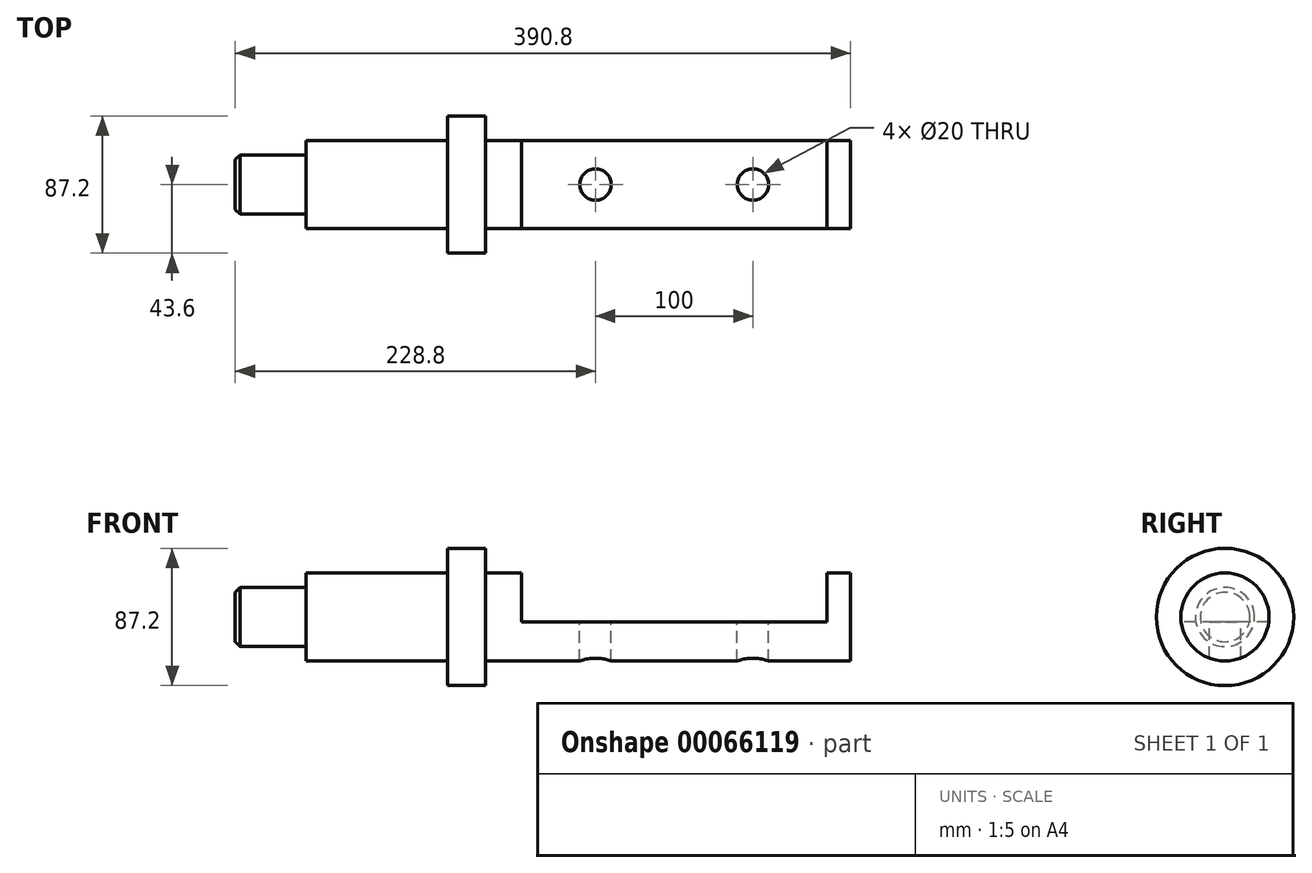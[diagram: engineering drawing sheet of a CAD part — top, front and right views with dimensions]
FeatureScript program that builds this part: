
annotation { "Feature Type Name" : "Feature", "Feature Type Description" : "" }
export const myFeature = defineFeature(function(context is Context, id is Id, definition is map)
    precondition{}
    {
        {
            var Q0;
            Q0=qCreatedBy(makeId("Front.planeOp"),FACE);
            var sketch = newSketch(context, id + "F0", { "sketchPlane" : qUnion([Q0])});
            skLineSegment(sketch, "E0", {"start": v(-158.8, 0) * mm, "end": v(-158.8, 18.75) * mm});
            skLineSegment(sketch, "E1", {"start": v(-158.8, 18.75) * mm, "end": v(-113.8, 18.75) * mm});
            skLineSegment(sketch, "E2", {"start": v(-113.8, 18.75) * mm, "end": v(-113.8, 28) * mm});
            skLineSegment(sketch, "E3", {"start": v(-113.8, 28) * mm, "end": v(-24, 28) * mm});
            skLineSegment(sketch, "E4", {"start": v(-24, 28) * mm, "end": v(-24, 43.6) * mm});
            skLineSegment(sketch, "E5", {"start": v(-24, 43.6) * mm, "end": v(0, 43.6) * mm});
            skLineSegment(sketch, "E6", {"start": v(0, 43.6) * mm, "end": v(0, 28) * mm});
            skLineSegment(sketch, "E7", {"start": v(0, 28) * mm, "end": v(232, 28) * mm});
            skLineSegment(sketch, "E8", {"start": v(232, 28) * mm, "end": v(232, 0) * mm});
            skLineSegment(sketch, "E9", {"start": v(232, 0) * mm, "end": v(-158.8, 0) * mm});
            skSolve(sketch);
        }
        {
            var Q0;
            Q0=makeQuery(id+"F0.imprint","IMPRINT",FACE,{"disambiguationData":[TD([[makeQuery(id+"F0.imprint","IMPRINT",EDGE,{"derivedFrom":sQuery(id+"F0.wireOp",EDGE,"E0")}),-1.0]])]});
            var Q1;
            Q1=sQuery(id+"F0.wireOp",EDGE,"E9");
            revolve(context, id + "F1", {"entities" : qUnion([Q0]), "axis" : qUnion([Q1]), "revolveType" : RevolveType.FULL});
        }
        {
            var Q0;
            Q0=qCreatedBy(makeId("Front.planeOp"),FACE);
            var sketch = newSketch(context, id + "F2", { "sketchPlane" : qUnion([Q0])});
            skLineSegment(sketch, "E10.bottom", {"start": v(23.1, 41.08) * mm, "end": v(216.9, 41.08) * mm});
            skLineSegment(sketch, "E10.top", {"start": v(23.1, -3.1) * mm, "end": v(216.9, -3.1) * mm});
            skLineSegment(sketch, "E10.left", {"start": v(23.1, 41.08) * mm, "end": v(23.1, -3.1) * mm});
            skLineSegment(sketch, "E10.right", {"start": v(216.9, 41.08) * mm, "end": v(216.9, -3.1) * mm});
            skLineSegment(sketch, "E11.0", {"start": v(232, 28) * mm, "end": v(232, -28) * mm, "construction": true});
            skSolve(sketch);
        }
        {
            var Q0;
            Q0=makeQuery(id+"F2.imprint","IMPRINT",FACE,{"disambiguationData":[TD([[makeQuery(id+"F2.imprint","IMPRINT",EDGE,{"derivedFrom":sQuery(id+"F2.wireOp",EDGE,"E10.bottom")}),-1.0]])]});
            extrude(context, id + "F3", {"entities" : qUnion([Q0]), "operationType" : NewBodyOperationType.REMOVE, "endBound" : BoundingType.THROUGH_ALL, "oppositeDirection" : true, "depth" : 25 * mm, "hasSecondDirection" : true, "secondDirectionBound" : SecondDirectionBoundingType.THROUGH_ALL, "secondDirectionOppositeDirection" : false, "secondDirectionDepth" : 25 * mm});
        }
        {
            var Q0;
            Q0=makeQuery(id+"F3.boolean.opBoolean","COPY",FACE,{"derivedFrom":makeQuery(id+"F3.opExtrude","SWEPT_FACE",FACE,{"disambiguationData":[OSD([sQuery(id+"F2.wireOp",EDGE,"E10.top")])]})});
            var sketch = newSketch(context, id + "F4", { "sketchPlane" : qUnion([Q0])});
            skPoint(sketch, "E12", {"position": v(70, 0) * mm});
            skPoint(sketch, "E13", {"position": v(170, 0) * mm});
            skSolve(sketch);
        }
        {
            var Q0;
            Q0=sQuery(id+"F4.wireOp",VERTEX,"E12");
            var Q1;
            Q1=sQuery(id+"F4.wireOp",VERTEX,"E13");
            var Q2;
            Q2=makeQuery(id+"F1.opRevolve","SWEPT_BODY",BODY,{"disambiguationData":[OSD([sQuery(id+"F0.wireOp",EDGE,"E0"),sQuery(id+"F0.wireOp",EDGE,"E1"),sQuery(id+"F0.wireOp",EDGE,"E2"),sQuery(id+"F0.wireOp",EDGE,"E3"),sQuery(id+"F0.wireOp",EDGE,"E4"),sQuery(id+"F0.wireOp",EDGE,"E5"),sQuery(id+"F0.wireOp",EDGE,"E6"),sQuery(id+"F0.wireOp",EDGE,"E7"),sQuery(id+"F0.wireOp",EDGE,"E8"),sQuery(id+"F0.wireOp",EDGE,"E9")])]});
            hole(context, id + "F5", {"style" : HoleStyle.SIMPLE, "holeDiameter" : 20 * mm, "endStyle" : HoleEndStyle.THROUGH, "locations" : qUnion([Q0, Q1]), "scope" : qUnion([Q2])});
        }
        {
            var Q0;
            Q0=makeQuery(id+"F1.opRevolve","SWEPT_FACE",FACE,{"disambiguationData":[OSD([sQuery(id+"F0.wireOp",EDGE,"E0")])]});
            chamfer(context, id + "F6", {"entities" : qUnion([Q0]), "width" : 3 * mm, "tangentPropagation" : true});
        }
    });
